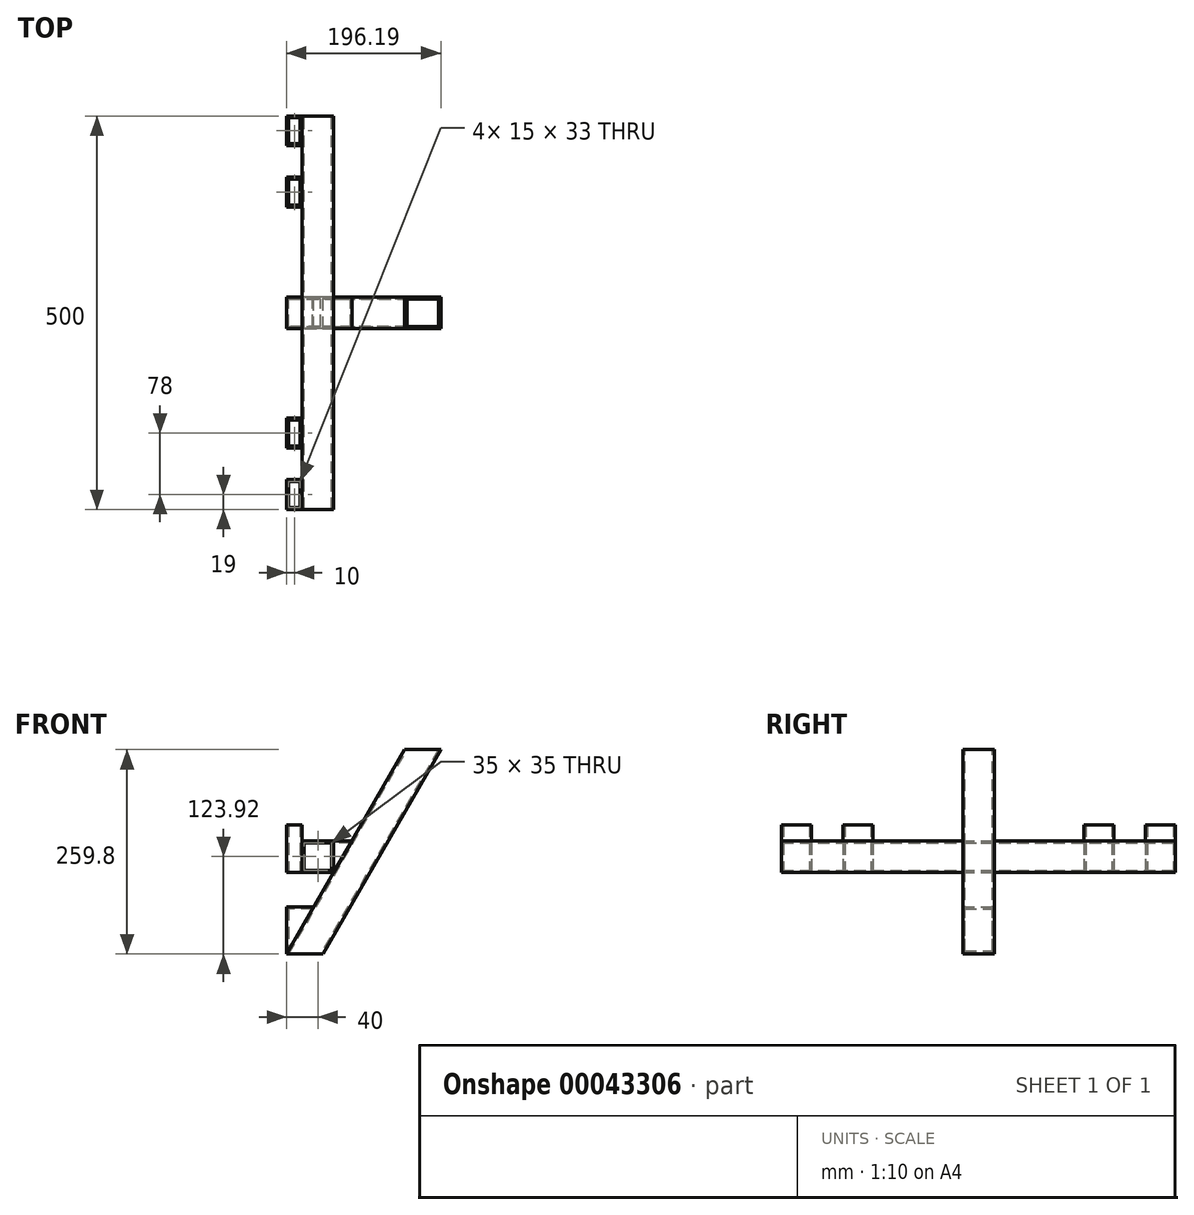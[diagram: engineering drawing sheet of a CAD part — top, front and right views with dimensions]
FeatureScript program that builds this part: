
annotation { "Feature Type Name" : "Feature", "Feature Type Description" : "" }
export const myFeature = defineFeature(function(context is Context, id is Id, definition is map)
    precondition{}
    {
        {
            var Q0;
            Q0=qCreatedBy(makeId("Top.planeOp"),FACE);
            var sketch = newSketch(context, id + "F0", { "sketchPlane" : qUnion([Q0])});
            skLineSegment(sketch, "E0.bottom", {"start": v(0, 250) * mm, "end": v(20, 250) * mm});
            skLineSegment(sketch, "E0.top", {"start": v(0, 212) * mm, "end": v(20, 212) * mm});
            skLineSegment(sketch, "E0.left", {"start": v(0, 250) * mm, "end": v(0, 212) * mm});
            skLineSegment(sketch, "E0.right", {"start": v(20, 250) * mm, "end": v(20, 212) * mm});
            skLineSegment(sketch, "E1.bottom", {"start": v(0, 172) * mm, "end": v(20, 172) * mm});
            skLineSegment(sketch, "E1.top", {"start": v(0, 134) * mm, "end": v(20, 134) * mm});
            skLineSegment(sketch, "E1.left", {"start": v(0, 172) * mm, "end": v(0, 134) * mm});
            skLineSegment(sketch, "E1.right", {"start": v(20, 172) * mm, "end": v(20, 134) * mm});
            skLineSegment(sketch, "E2", {"start": v(0, 0) * mm, "end": v(274, 0) * mm, "construction": true});
            skLineSegment(sketch, "E3.MirrorCS", {"start": v(0, -250) * mm, "end": v(20, -250) * mm});
            skLineSegment(sketch, "E4.MirrorCS", {"start": v(0, -212) * mm, "end": v(20, -212) * mm});
            skLineSegment(sketch, "E5.MirrorCS", {"start": v(20, -172) * mm, "end": v(20, -134) * mm});
            skLineSegment(sketch, "E6.MirrorCS", {"start": v(0, -172) * mm, "end": v(0, -134) * mm});
            skLineSegment(sketch, "E7.MirrorCS", {"start": v(0, -134) * mm, "end": v(20, -134) * mm});
            skLineSegment(sketch, "E8.MirrorCS", {"start": v(0, -172) * mm, "end": v(20, -172) * mm});
            skLineSegment(sketch, "E9.MirrorCS", {"start": v(20, -250) * mm, "end": v(20, -212) * mm});
            skLineSegment(sketch, "E10.MirrorCS", {"start": v(0, -250) * mm, "end": v(0, -212) * mm});
            skSolve(sketch);
        }
        {
            var Q0;
            Q0 = qSketchRegion(id + "F0", true);
            extrude(context, id + "F1", {"entities" : qUnion([Q0]), "depth" : 60 * mm});
        }
        {
            var Q0;
            Q0=makeQuery(id+"F1.opExtrude","CAP_FACE",FACE,{"disambiguationData":[OSD([sQuery(id+"F0.wireOp",EDGE,"E3.MirrorCS"),sQuery(id+"F0.wireOp",EDGE,"E4.MirrorCS"),sQuery(id+"F0.wireOp",EDGE,"E9.MirrorCS"),sQuery(id+"F0.wireOp",EDGE,"E10.MirrorCS")])],"isStart":false});
            var Q1;
            Q1=makeQuery(id+"F1.opExtrude","CAP_FACE",FACE,{"disambiguationData":[OSD([sQuery(id+"F0.wireOp",EDGE,"E3.MirrorCS"),sQuery(id+"F0.wireOp",EDGE,"E4.MirrorCS"),sQuery(id+"F0.wireOp",EDGE,"E9.MirrorCS"),sQuery(id+"F0.wireOp",EDGE,"E10.MirrorCS")])],"isStart":true});
            var Q2;
            Q2=makeQuery(id+"F1.opExtrude","CAP_FACE",FACE,{"disambiguationData":[OSD([sQuery(id+"F0.wireOp",EDGE,"E5.MirrorCS"),sQuery(id+"F0.wireOp",EDGE,"E6.MirrorCS"),sQuery(id+"F0.wireOp",EDGE,"E7.MirrorCS"),sQuery(id+"F0.wireOp",EDGE,"E8.MirrorCS")])],"isStart":false});
            var Q3;
            Q3=makeQuery(id+"F1.opExtrude","CAP_FACE",FACE,{"disambiguationData":[OSD([sQuery(id+"F0.wireOp",EDGE,"E1.bottom"),sQuery(id+"F0.wireOp",EDGE,"E1.top"),sQuery(id+"F0.wireOp",EDGE,"E1.left"),sQuery(id+"F0.wireOp",EDGE,"E1.right")])],"isStart":false});
            var Q4;
            Q4=makeQuery(id+"F1.opExtrude","CAP_FACE",FACE,{"disambiguationData":[OSD([sQuery(id+"F0.wireOp",EDGE,"E0.bottom"),sQuery(id+"F0.wireOp",EDGE,"E0.top"),sQuery(id+"F0.wireOp",EDGE,"E0.left"),sQuery(id+"F0.wireOp",EDGE,"E0.right")])],"isStart":false});
            var Q5;
            Q5=makeQuery(id+"F1.opExtrude","CAP_FACE",FACE,{"disambiguationData":[OSD([sQuery(id+"F0.wireOp",EDGE,"E5.MirrorCS"),sQuery(id+"F0.wireOp",EDGE,"E6.MirrorCS"),sQuery(id+"F0.wireOp",EDGE,"E7.MirrorCS"),sQuery(id+"F0.wireOp",EDGE,"E8.MirrorCS")])],"isStart":true});
            var Q6;
            Q6=makeQuery(id+"F1.opExtrude","CAP_FACE",FACE,{"disambiguationData":[OSD([sQuery(id+"F0.wireOp",EDGE,"E1.bottom"),sQuery(id+"F0.wireOp",EDGE,"E1.top"),sQuery(id+"F0.wireOp",EDGE,"E1.left"),sQuery(id+"F0.wireOp",EDGE,"E1.right")])],"isStart":true});
            var Q7;
            Q7=makeQuery(id+"F1.opExtrude","CAP_FACE",FACE,{"disambiguationData":[OSD([sQuery(id+"F0.wireOp",EDGE,"E0.bottom"),sQuery(id+"F0.wireOp",EDGE,"E0.top"),sQuery(id+"F0.wireOp",EDGE,"E0.left"),sQuery(id+"F0.wireOp",EDGE,"E0.right")])],"isStart":true});
            var Q8;
            Q8=makeQuery(id+"F1.opExtrude","SWEPT_BODY",BODY,{"disambiguationData":[OSD([sQuery(id+"F0.wireOp",EDGE,"E5.MirrorCS"),sQuery(id+"F0.wireOp",EDGE,"E6.MirrorCS"),sQuery(id+"F0.wireOp",EDGE,"E7.MirrorCS"),sQuery(id+"F0.wireOp",EDGE,"E8.MirrorCS")])]});
            shell(context, id + "F2", {"entities" : qUnion([Q0, Q1, Q2, Q3, Q4, Q5, Q6, Q7]), "parts" : qUnion([Q8]), "thickness" : 2.5 * mm});
        }
        {
            var Q0;
            Q0=qCreatedBy(makeId("Front.planeOp"),FACE);
            var sketch = newSketch(context, id + "F3", { "sketchPlane" : qUnion([Q0])});
            skLineSegment(sketch, "E11.bottom", {"start": v(20, 0) * mm, "end": v(60, 0) * mm});
            skLineSegment(sketch, "E11.top", {"start": v(20, 40) * mm, "end": v(60, 40) * mm});
            skLineSegment(sketch, "E11.left", {"start": v(20, 0) * mm, "end": v(20, 40) * mm});
            skLineSegment(sketch, "E11.right", {"start": v(60, 0) * mm, "end": v(60, 40) * mm});
            skSolve(sketch);
        }
        {
            var Q0;
            Q0 = qSketchRegion(id + "F3", true);
            extrude(context, id + "F4", {"entities" : qUnion([Q0]), "depth" : 250 * mm, "hasSecondDirection" : true, "secondDirectionOppositeDirection" : true, "secondDirectionDepth" : 250 * mm});
        }
        {
            var Q0;
            Q0=makeQuery(id+"F4.opExtrude","CAP_FACE",FACE,{"disambiguationData":[OSD([sQuery(id+"F3.wireOp",EDGE,"E11.bottom"),sQuery(id+"F3.wireOp",EDGE,"E11.top"),sQuery(id+"F3.wireOp",EDGE,"E11.left"),sQuery(id+"F3.wireOp",EDGE,"E11.right")])],"isStart":false});
            var Q1;
            Q1=makeQuery(id+"F4.opExtrude","CAP_FACE",FACE,{"disambiguationData":[OSD([sQuery(id+"F3.wireOp",EDGE,"E11.bottom"),sQuery(id+"F3.wireOp",EDGE,"E11.top"),sQuery(id+"F3.wireOp",EDGE,"E11.left"),sQuery(id+"F3.wireOp",EDGE,"E11.right")])],"isStart":true});
            shell(context, id + "F5", {"entities" : qUnion([Q0, Q1]), "thickness" : 2.5 * mm});
        }
        {
            var Q0;
            Q0=qCreatedBy(makeId("Front.planeOp"),FACE);
            var sketch = newSketch(context, id + "F6", { "sketchPlane" : qUnion([Q0])});
            skLineSegment(sketch, "E12", {"start": v(0, -103.92) * mm, "end": v(150, 155.88) * mm});
            skLineSegment(sketch, "E13", {"start": v(150, 155.88) * mm, "end": v(196.19, 155.88) * mm});
            skLineSegment(sketch, "E14", {"start": v(196.19, 155.88) * mm, "end": v(46.19, -103.92) * mm});
            skLineSegment(sketch, "E15", {"start": v(46.19, -103.92) * mm, "end": v(0, -103.92) * mm});
            skLineSegment(sketch, "E16", {"start": v(0, 0) * mm, "end": v(0, -103.92) * mm, "construction": true});
            skSolve(sketch);
        }
        {
            var Q0;
            Q0=makeQuery(id+"F6.imprint","IMPRINT",FACE,{"disambiguationData":[TD([[makeQuery(id+"F6.imprint","IMPRINT",EDGE,{"derivedFrom":sQuery(id+"F6.wireOp",EDGE,"E12")}),-1.0]])]});
            extrude(context, id + "F7", {"entities" : qUnion([Q0]), "depth" : 20 * mm, "hasSecondDirection" : true, "secondDirectionOppositeDirection" : true, "secondDirectionDepth" : 20 * mm});
        }
        {
            var Q0;
            Q0=makeQuery(id+"F7.opExtrude","SWEPT_FACE",FACE,{"disambiguationData":[OSD([sQuery(id+"F6.wireOp",EDGE,"E15")])]});
            var Q1;
            Q1=makeQuery(id+"F7.opExtrude","SWEPT_FACE",FACE,{"disambiguationData":[OSD([sQuery(id+"F6.wireOp",EDGE,"E13")])]});
            shell(context, id + "F8", {"entities" : qUnion([Q0, Q1]), "thickness" : 2.5 * mm});
        }
        {
            var Q0;
            Q0=qCreatedBy(makeId("Front.planeOp"),FACE);
            var sketch = newSketch(context, id + "F9", { "sketchPlane" : qUnion([Q0])});
            skLineSegment(sketch, "E17", {"start": v(0, -43.92) * mm, "end": v(0, -103.92) * mm});
            skLineSegment(sketch, "E18", {"start": v(0, -103.92) * mm, "end": v(34.64, -43.92) * mm});
            skLineSegment(sketch, "E19", {"start": v(34.64, -43.92) * mm, "end": v(0, -43.92) * mm});
            skSolve(sketch);
        }
        {
            var Q0;
            Q0 = qSketchRegion(id + "F9", true);
            extrude(context, id + "F10", {"entities" : qUnion([Q0]), "depth" : 20 * mm, "hasSecondDirection" : true, "secondDirectionOppositeDirection" : true, "secondDirectionDepth" : 20 * mm});
        }
        {
            var Q0;
            Q0=makeQuery(id+"F10.opExtrude","SWEPT_FACE",FACE,{"disambiguationData":[OSD([sQuery(id+"F9.wireOp",EDGE,"E18")])]});
            shell(context, id + "F11", {"entities" : qUnion([Q0]), "thickness" : 2.5 * mm});
        }
        {
            var Q0;
            Q0=qCreatedBy(makeId("Front.planeOp"),FACE);
            var sketch = newSketch(context, id + "F12", { "sketchPlane" : qUnion([Q0])});
            skLineSegment(sketch, "E20", {"start": v(60, 40) * mm, "end": v(60, 0) * mm});
            skLineSegment(sketch, "E21", {"start": v(60, 0) * mm, "end": v(83.1, 40) * mm});
            skLineSegment(sketch, "E22", {"start": v(83.1, 40) * mm, "end": v(60, 40) * mm});
            skSolve(sketch);
        }
        {
            var Q0;
            Q0 = qSketchRegion(id + "F12", true);
            extrude(context, id + "F13", {"entities" : qUnion([Q0]), "depth" : 20 * mm, "hasSecondDirection" : true, "secondDirectionOppositeDirection" : true, "secondDirectionDepth" : 20 * mm});
        }
        {
            var Q0;
            Q0=makeQuery(id+"F13.opExtrude","SWEPT_FACE",FACE,{"disambiguationData":[OSD([sQuery(id+"F12.wireOp",EDGE,"E21")])]});
            var Q1;
            Q1=makeQuery(id+"F13.opExtrude","SWEPT_FACE",FACE,{"disambiguationData":[OSD([sQuery(id+"F12.wireOp",EDGE,"E20")])]});
            shell(context, id + "F14", {"entities" : qUnion([Q0, Q1]), "thickness" : 2.5 * mm});
        }
    });
